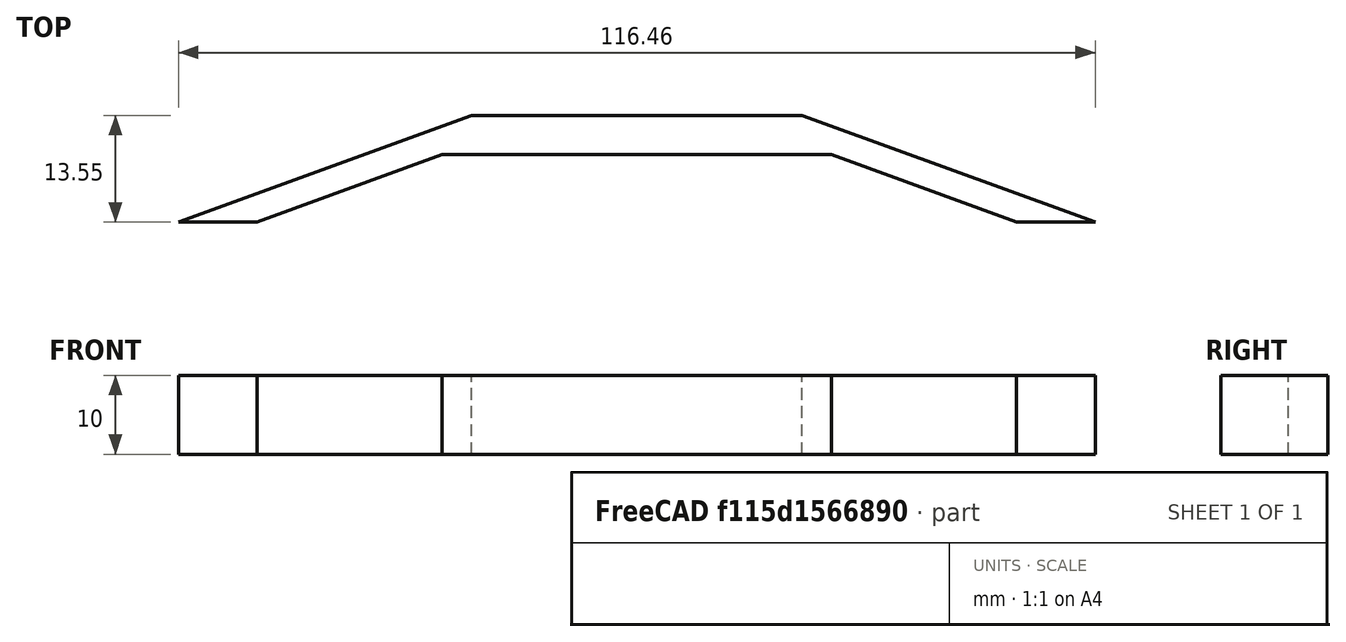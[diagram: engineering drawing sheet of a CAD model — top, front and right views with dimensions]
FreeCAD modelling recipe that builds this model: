
FCSTD DOCUMENT  (FreeCAD 0.20R29410 (Git))
Label: ultrasonicHolder
License: All rights reserved
LicenseURL: http://en.wikipedia.org/wiki/All_rights_reserved
objects: Sketcher::SketchObject×1, PartDesign::Pad×1, PartDesign::Body×1
note: 4 computed .brp shape members not serialized (recipe doc carries the construction recipe); baked Part::Feature solids carry a one-line shape summary decoded from their .brp

FEATURE [Sketcher::SketchObject] Sketch
  FullyConstrained = true
  MapMode = 5
  Support = -> [XY_Plane]
  sketch-geometry (8):
    g0: LineSegment StartX=0 StartY=0 StartZ=0 EndX=37.2297 EndY=13.5505 EndZ=0
    g1: LineSegment StartX=37.2297 StartY=13.5505 StartZ=0 EndX=79.2297 EndY=13.5505 EndZ=0
    g2: LineSegment StartX=79.2297 StartY=13.5505 StartZ=0 EndX=116.459 EndY=0 EndZ=0
    g3: LineSegment StartX=116.459 StartY=5e-16 StartZ=0 EndX=106.459 EndY=5e-16 EndZ=0
    g4: LineSegment StartX=106.459 StartY=5e-16 StartZ=0 EndX=82.9671 EndY=8.5505 EndZ=0
    g5: LineSegment StartX=82.9671 StartY=8.5505 StartZ=0 EndX=33.4923 EndY=8.5505 EndZ=0
    g6: LineSegment StartX=33.4923 StartY=8.5505 StartZ=0 EndX=10 EndY=0 EndZ=0
    g7: LineSegment StartX=0 StartY=0 StartZ=0 EndX=10 EndY=0 EndZ=0
  constraints (23):
    c: Coincident(g0,g1)
    c: Horizontal(g1)
    c: Coincident(g1,g2)
    c: Coincident(g2,g3)
    c: Horizontal(g3)
    c: Coincident(g3,g4)
    c: Coincident(g4,g5)
    c: Horizontal(g5)
    c: Coincident(g5,g6)
    c: DistanceX(g1,g1) = 42
    c: DistanceY(g5,g0) = 5
    c: Equal(g2,g0)
    c: Equal(g4,g6)
    c: DistanceX(g3,g3) = 10
    c: Parallel(g4,g2)
    c: Parallel(g6,g0)
    c: Coincident(g7,g0)
    c: Coincident(g7,g6)
    c: Horizontal(g7)
    c: DistanceX(g7,g7) = 10
    c: Angle(g5,g4) = 2.79253
    c: Distance(g4,g3) = 25
    c: Coincident(g-1,g0)
FEATURE [PartDesign::Pad] Pad
  Direction = (0,0,1)
  Length = 10
  Length2 = 10
  Profile = -> Sketch
  ReferenceAxis = -> Sketch [N_Axis]
  Type = 0
FEATURE [PartDesign::Body] Body
  Group = -> [Sketch,Pad]
  Origin = -> Origin
  Tip = -> Pad
